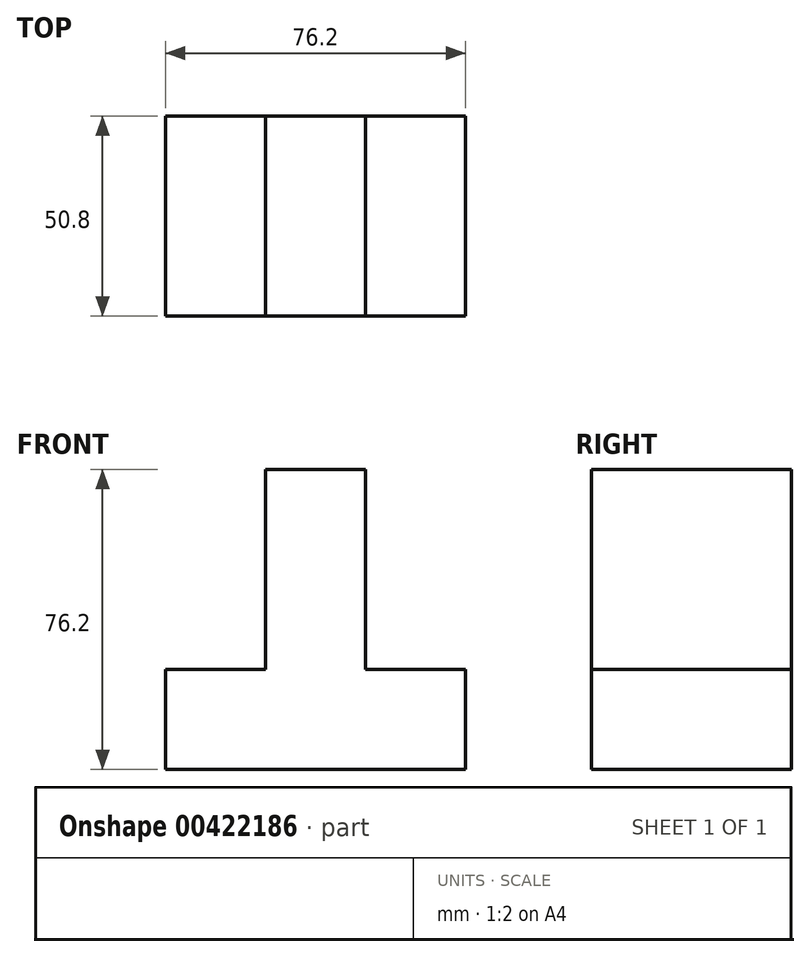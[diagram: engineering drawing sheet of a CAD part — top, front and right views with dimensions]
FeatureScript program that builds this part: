
annotation { "Feature Type Name" : "Feature", "Feature Type Description" : "" }
export const myFeature = defineFeature(function(context is Context, id is Id, definition is map)
    precondition{}
    {
        {
            var Q0;
            Q0=qCreatedBy(makeId("Front.planeOp"),FACE);
            var sketch = newSketch(context, id + "F0", { "sketchPlane" : qUnion([Q0])});
            skLineSegment(sketch, "E0", {"start": v(-50.8, -48.5) * mm, "end": v(25.4, -48.5) * mm});
            skLineSegment(sketch, "E1", {"start": v(-50.8, -48.5) * mm, "end": v(-50.8, -23.1) * mm});
            skLineSegment(sketch, "E2", {"start": v(-50.8, -23.1) * mm, "end": v(-25.4, -23.1) * mm});
            skLineSegment(sketch, "E3", {"start": v(-25.4, -23.1) * mm, "end": v(-25.4, 27.7) * mm});
            skLineSegment(sketch, "E4", {"start": v(25.4, -48.5) * mm, "end": v(25.4, -23.1) * mm});
            skLineSegment(sketch, "E5", {"start": v(25.4, -23.1) * mm, "end": v(0, -23.1) * mm});
            skLineSegment(sketch, "E6", {"start": v(0, -23.1) * mm, "end": v(0, 27.7) * mm});
            skLineSegment(sketch, "E7", {"start": v(0, 27.7) * mm, "end": v(-25.4, 27.7) * mm});
            skSolve(sketch);
        }
        {
            var Q0;
            Q0=makeQuery(id+"F0.imprint","IMPRINT",FACE,{"disambiguationData":[TD([[makeQuery(id+"F0.imprint","IMPRINT",EDGE,{"derivedFrom":sQuery(id+"F0.wireOp",EDGE,"E0")}),1.0]])]});
            extrude(context, id + "F1", {"entities" : qUnion([Q0]), "depth" : 50.8 * mm});
        }
    });
